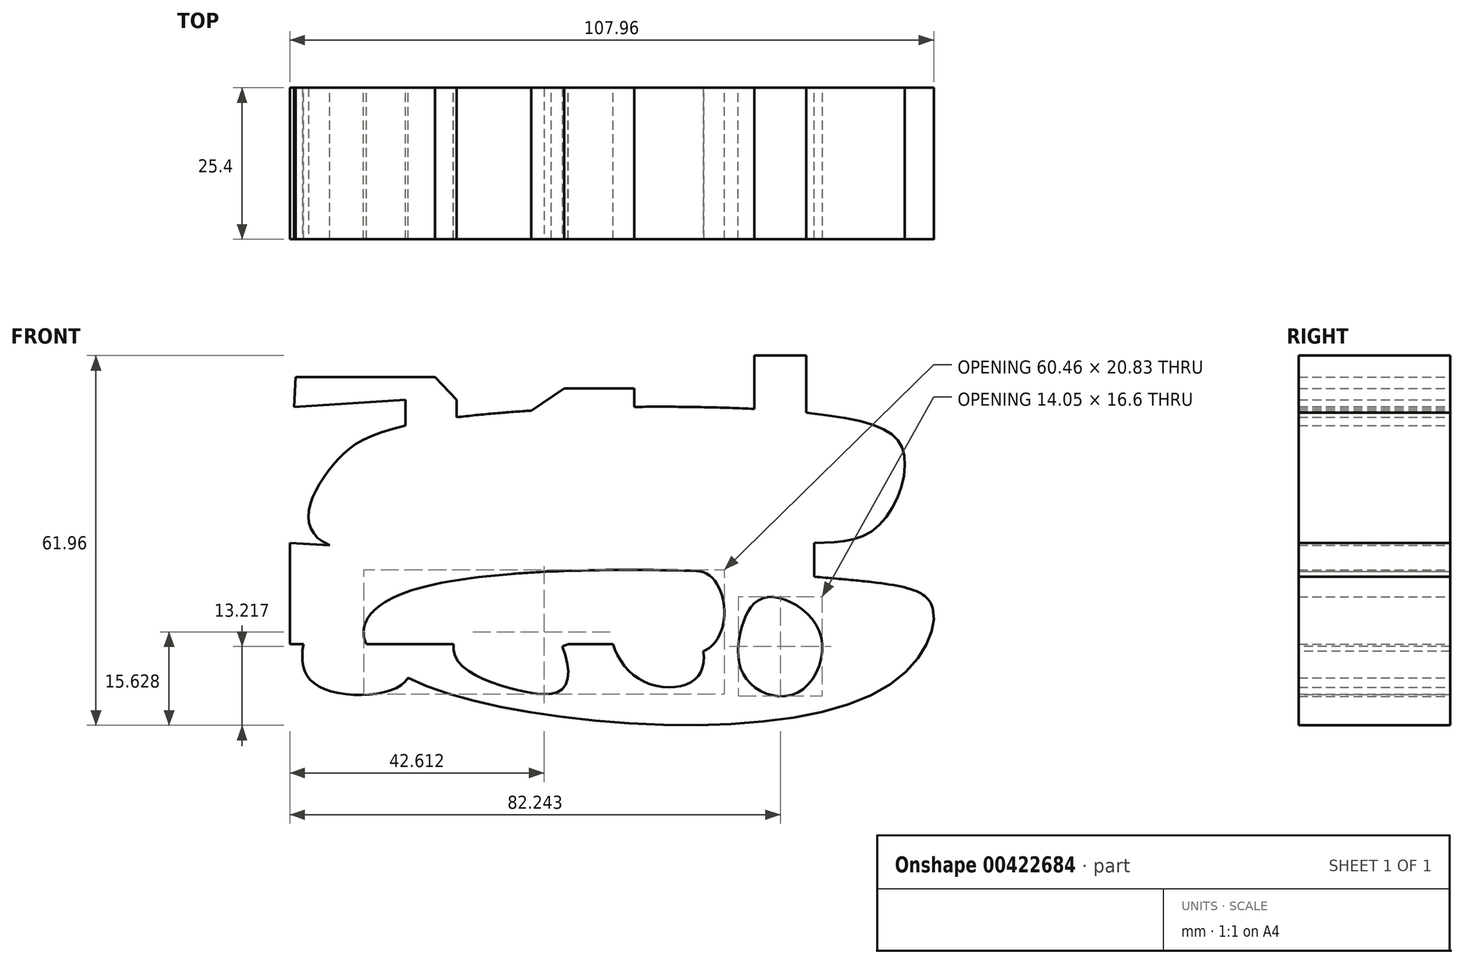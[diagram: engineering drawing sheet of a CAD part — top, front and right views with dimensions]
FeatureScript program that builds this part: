
annotation { "Feature Type Name" : "Feature", "Feature Type Description" : "" }
export const myFeature = defineFeature(function(context is Context, id is Id, definition is map)
    precondition{}
    {
        {
            var Q0;
            Q0=qCreatedBy(makeId("Front.planeOp"),FACE);
            var sketch = newSketch(context, id + "F0", { "sketchPlane" : qUnion([Q0])});
            skFitSpline(sketch, "E0", {"points": [v(54.86, -13.9) * mm, v(-13.41, -15.33) * mm, v(-31.38, -4.8) * mm, v(-23.24, 3.11) * mm, v(52.7, 4.55) * mm, v(63.96, 0) * mm, v(54.86, -13.9) * mm]});
            skLineSegment(sketch, "E1", {"start": v(-6.64, 5.8) * mm, "end": v(-6.64, 10.59) * mm});
            skLineSegment(sketch, "E2", {"start": v(-6.64, 10.59) * mm, "end": v(44.08, 10.59) * mm});
            skLineSegment(sketch, "E3", {"start": v(44.08, 11.02) * mm, "end": v(44.08, 5.33) * mm});
            skFitSpline(sketch, "E4", {"points": [v(-6.64, 10.59) * mm, v(-37.13, 10.59) * mm, v(-40.72, 15.57) * mm, v(-36.9, 23.72) * mm, v(-24.43, 30.66) * mm, v(48.39, 32.1) * mm, v(59.17, 25.63) * mm, v(54.62, 13.65) * mm, v(44.08, 11.02) * mm], "startDerivative": vector(-228.12, -21.8) * mm, "endDerivative": vector(-117.55, -1.98) * mm});
            skLineSegment(sketch, "E5", {"start": v(-9.33, 32.73) * mm, "end": v(-9.33, 38.82) * mm});
            skLineSegment(sketch, "E6", {"start": v(13.9, 33.8) * mm, "end": v(13.9, 46.35) * mm});
            skLineSegment(sketch, "E7", {"start": v(21.78, 33.81) * mm, "end": v(21.78, 40.52) * mm});
            skLineSegment(sketch, "E8", {"start": v(42.76, 32.82) * mm, "end": v(42.76, 42.4) * mm});
            skLineSegment(sketch, "E9", {"start": v(42.76, 42.4) * mm, "end": v(34.02, 42.4) * mm});
            skLineSegment(sketch, "E10", {"start": v(34.02, 42.4) * mm, "end": v(34.02, 33.45) * mm});
            skFitSpline(sketch, "E11", {"points": [v(24.21, 6.33) * mm, v(28.99, 0) * mm, v(24.67, -7.43) * mm, v(14.61, -2.16) * mm, v(24.21, 6.33) * mm]});
            skLineSegment(sketch, "E12", {"start": v(-6.64, 5.8) * mm, "end": v(-43.84, 5.8) * mm});
            skLineSegment(sketch, "E13", {"start": v(-43.84, 5.8) * mm, "end": v(-43.84, 11.02) * mm});
            skLineSegment(sketch, "E14", {"start": v(-44.56, 11.02) * mm, "end": v(-37.13, 10.59) * mm});
            skPoint(sketch, "E15.6.internal.snap0", {"position": v(-25.24, 5.8) * mm});
            skFitSpline(sketch, "E15", {"points": [v(1.2, 6.26) * mm, v(7.43, 0) * mm, v(2.16, -6.23) * mm, v(-10.06, -4.07) * mm, v(-9.58, 2.16) * mm, v(0, 6.2) * mm, v(0, 5.8) * mm], "startDerivative": vector(47.28, -29.62) * mm, "endDerivative": vector(-5.21, -12.12) * mm});
            skPoint(sketch, "E16.1.internal.orphan", {"position": v(56.3, 4.55) * mm});
            skLineSegment(sketch, "E17", {"start": v(-43.84, 5.8) * mm, "end": v(-43.84, -5.99) * mm});
            skLineSegment(sketch, "E18", {"start": v(-43.84, -5.99) * mm, "end": v(53.66, -5.99) * mm});
            skLineSegment(sketch, "E19", {"start": v(53.66, -5.99) * mm, "end": v(53.66, 12.46) * mm});
            skFitSpline(sketch, "E20", {"points": [v(-35.93, 3.35) * mm, v(-27.55, -2.16) * mm, v(-24.43, -12.22) * mm, v(-39.53, -12.7) * mm, v(-40.96, -3.6) * mm, v(-35.93, 3.35) * mm]});
            skFitSpline(sketch, "E21", {"points": [v(-9.58, 2.16) * mm, v(0, -3.11) * mm, v(2.16, -13.18) * mm, v(-6.64, -13.41) * mm, v(-16.05, -8.14) * mm, v(-14.85, -1.92) * mm, v(-9.58, 2.16) * mm]});
            skFitSpline(sketch, "E22", {"points": [v(16.53, 2.16) * mm, v(23.48, -2.16) * mm, v(24.67, -11.26) * mm, v(14.61, -11.74) * mm, v(10.06, -2.16) * mm, v(14.61, 2.16) * mm], "startDerivative": vector(40.03, -14.62) * mm, "endDerivative": vector(35.7, 19.18) * mm});
            skFitSpline(sketch, "E23", {"points": [v(36.17, 1.92) * mm, v(45.04, -4.07) * mm, v(41.2, -14.13) * mm, v(32.82, -11.98) * mm, v(31.86, -3.35) * mm, v(36.17, 1.92) * mm]});
            skLineSegment(sketch, "E24", {"start": v(53.66, -2.64) * mm, "end": v(62.76, -2.64) * mm});
            skLineSegment(sketch, "E25", {"start": v(62.76, -2.64) * mm, "end": v(63.96, 0) * mm});
            skLineSegment(sketch, "E26", {"start": v(63.72, 0) * mm, "end": v(53.66, 0) * mm});
            skPoint(sketch, "E27.start.orphan", {"position": v(-24.44, 35) * mm});
            skPoint(sketch, "E28.end.orphan", {"position": v(-20.77, 35) * mm});
            skLineSegment(sketch, "E29", {"start": v(-19.52, 31.56) * mm, "end": v(-19.52, 35) * mm});
            skLineSegment(sketch, "E30", {"start": v(-19.52, 35) * mm, "end": v(-24.44, 35) * mm});
            skLineSegment(sketch, "E31", {"start": v(-24.44, 35) * mm, "end": v(-24.43, 30.66) * mm});
            skLineSegment(sketch, "E32", {"start": v(-19.52, 35) * mm, "end": v(-19.52, 38.82) * mm});
            skLineSegment(sketch, "E33", {"start": v(-19.52, 38.82) * mm, "end": v(-42.88, 38.82) * mm});
            skLineSegment(sketch, "E34", {"start": v(-42.88, 38.82) * mm, "end": v(-43.12, 33.78) * mm});
            skLineSegment(sketch, "E35", {"start": v(-43.12, 33.78) * mm, "end": v(-24.44, 35) * mm});
            skLineSegment(sketch, "E36", {"start": v(-19.52, 35) * mm, "end": v(-15.9, 32.06) * mm});
            skLineSegment(sketch, "E37", {"start": v(-15.9, 32.06) * mm, "end": v(-15.9, 35) * mm});
            skLineSegment(sketch, "E38", {"start": v(-15.9, 35) * mm, "end": v(-19.52, 38.82) * mm});
            skLineSegment(sketch, "E39", {"start": v(-3.35, 33.18) * mm, "end": v(2.15, 36.9) * mm});
            skLineSegment(sketch, "E40", {"start": v(2.15, 36.9) * mm, "end": v(13.9, 36.9) * mm});
            skSolve(sketch);
        }
        {
            var Q0;
            Q0 = qSketchRegion(id + "F0", true);
            extrude(context, id + "F1", {"entities" : qUnion([Q0]), "depth" : 25.4 * mm});
        }
    });
